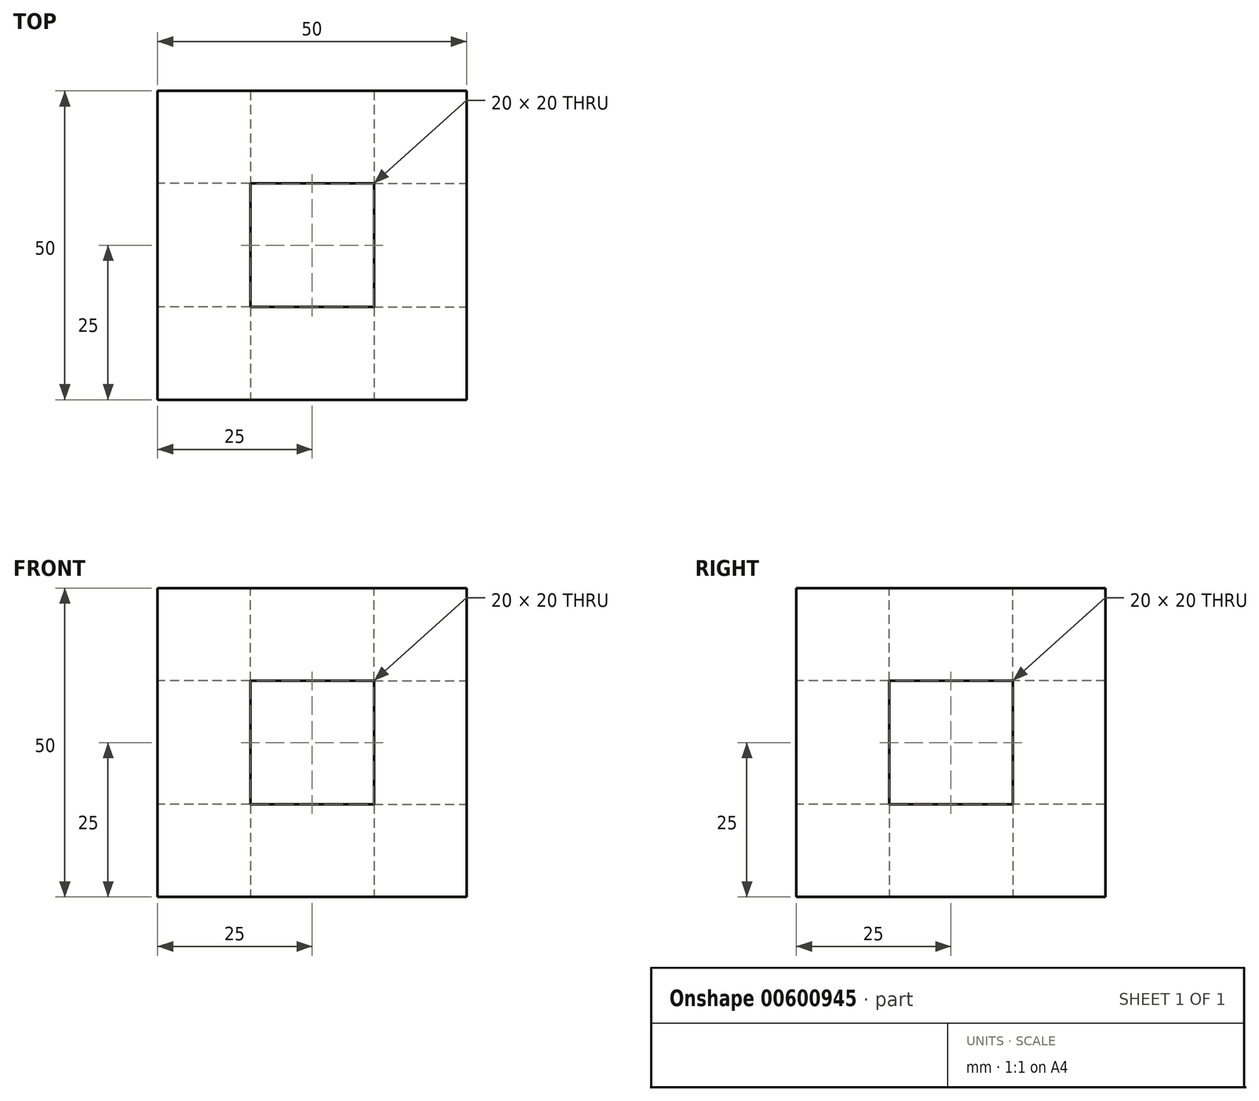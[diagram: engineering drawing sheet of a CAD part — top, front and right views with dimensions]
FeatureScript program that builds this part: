
annotation { "Feature Type Name" : "Feature", "Feature Type Description" : "" }
export const myFeature = defineFeature(function(context is Context, id is Id, definition is map)
    precondition{}
    {
        {
            var Q0;
            Q0=qCreatedBy(makeId("Front.planeOp"),FACE);
            var sketch = newSketch(context, id + "F0", { "sketchPlane" : qUnion([Q0])});
            skLineSegment(sketch, "E0.bottom", {"start": v(25, -25) * mm, "end": v(-25, -25) * mm});
            skLineSegment(sketch, "E0.top", {"start": v(25, 25) * mm, "end": v(-25, 25) * mm});
            skLineSegment(sketch, "E0.left", {"start": v(25, -25) * mm, "end": v(25, 25) * mm});
            skLineSegment(sketch, "E0.right", {"start": v(-25, -25) * mm, "end": v(-25, 25) * mm});
            skPoint(sketch, "E0.middle", {"position": v(0, 0) * mm});
            skSolve(sketch);
        }
        {
            var Q0;
            Q0 = qSketchRegion(id + "F0", true);
            extrude(context, id + "F1", {"entities" : qUnion([Q0]), "endBound" : BoundingType.SYMMETRIC, "depth" : 50 * mm, "offsetDistance" : 25 * mm});
        }
        {
            var Q0;
            Q0=makeQuery(id+"F1.opExtrude","CAP_FACE",FACE,{"disambiguationData":[OSD([sQuery(id+"F0.wireOp",EDGE,"E0.bottom"),sQuery(id+"F0.wireOp",EDGE,"E0.top"),sQuery(id+"F0.wireOp",EDGE,"E0.left"),sQuery(id+"F0.wireOp",EDGE,"E0.right")])],"isStart":false});
            var sketch = newSketch(context, id + "F2", { "sketchPlane" : qUnion([Q0])});
            skLineSegment(sketch, "E1.bottom", {"start": v(10, -10) * mm, "end": v(-10, -10) * mm});
            skLineSegment(sketch, "E1.top", {"start": v(10, 10) * mm, "end": v(-10, 10) * mm});
            skLineSegment(sketch, "E1.left", {"start": v(10, -10) * mm, "end": v(10, 10) * mm});
            skLineSegment(sketch, "E1.right", {"start": v(-10, -10) * mm, "end": v(-10, 10) * mm});
            skPoint(sketch, "E1.middle", {"position": v(0, 0) * mm});
            skSolve(sketch);
        }
        {
            var Q0;
            Q0=makeQuery(id+"F2.imprint","IMPRINT",FACE,{"disambiguationData":[TD([[makeQuery(id+"F2.imprint","IMPRINT",EDGE,{"derivedFrom":sQuery(id+"F2.wireOp",EDGE,"E1.bottom")}),-1.0]])]});
            extrude(context, id + "F3", {"entities" : qUnion([Q0]), "operationType" : NewBodyOperationType.REMOVE, "endBound" : BoundingType.UP_TO_NEXT, "oppositeDirection" : true, "depth" : 25 * mm, "offsetDistance" : 25 * mm});
        }
        {
            var Q0;
            Q0=makeQuery(id+"F1.opExtrude","SWEPT_FACE",FACE,{"disambiguationData":[OSD([sQuery(id+"F0.wireOp",EDGE,"E0.right")])]});
            var sketch = newSketch(context, id + "F4", { "sketchPlane" : qUnion([Q0])});
            skLineSegment(sketch, "E2.bottom", {"start": v(10, -10) * mm, "end": v(-10, -10) * mm});
            skLineSegment(sketch, "E2.top", {"start": v(10, 10) * mm, "end": v(-10, 10) * mm});
            skLineSegment(sketch, "E2.left", {"start": v(10, -10) * mm, "end": v(10, 10) * mm});
            skLineSegment(sketch, "E2.right", {"start": v(-10, -10) * mm, "end": v(-10, 10) * mm});
            skPoint(sketch, "E2.middle", {"position": v(0, 0) * mm});
            skSolve(sketch);
        }
        {
            var Q0;
            Q0 = qSketchRegion(id + "F4", true);
            extrude(context, id + "F5", {"entities" : qUnion([Q0]), "operationType" : NewBodyOperationType.REMOVE, "endBound" : BoundingType.UP_TO_NEXT, "oppositeDirection" : true, "depth" : 25 * mm, "offsetDistance" : 25 * mm});
        }
        {
            var Q0;
            Q0=makeQuery(id+"F1.opExtrude","SWEPT_FACE",FACE,{"disambiguationData":[OSD([sQuery(id+"F0.wireOp",EDGE,"E0.left")])]});
            var sketch = newSketch(context, id + "F6", { "sketchPlane" : qUnion([Q0])});
            skLineSegment(sketch, "E3.bottom", {"start": v(10, -10) * mm, "end": v(-10, -10) * mm});
            skLineSegment(sketch, "E3.top", {"start": v(10, 10) * mm, "end": v(-10, 10) * mm});
            skLineSegment(sketch, "E3.left", {"start": v(10, -10) * mm, "end": v(10, 10) * mm});
            skLineSegment(sketch, "E3.right", {"start": v(-10, -10) * mm, "end": v(-10, 10) * mm});
            skPoint(sketch, "E3.middle", {"position": v(0, 0) * mm});
            skSolve(sketch);
        }
        {
            var Q0;
            Q0 = qSketchRegion(id + "F6", true);
            extrude(context, id + "F7", {"entities" : qUnion([Q0]), "operationType" : NewBodyOperationType.REMOVE, "endBound" : BoundingType.UP_TO_NEXT, "oppositeDirection" : true, "depth" : 25 * mm, "offsetDistance" : 25 * mm});
        }
        {
            var Q0;
            Q0=makeQuery(id+"F1.opExtrude","SWEPT_FACE",FACE,{"disambiguationData":[OSD([sQuery(id+"F0.wireOp",EDGE,"E0.top")])]});
            var sketch = newSketch(context, id + "F8", { "sketchPlane" : qUnion([Q0])});
            skLineSegment(sketch, "E4.bottom", {"start": v(10, -10) * mm, "end": v(-10, -10) * mm});
            skLineSegment(sketch, "E4.top", {"start": v(10, 10) * mm, "end": v(-10, 10) * mm});
            skLineSegment(sketch, "E4.left", {"start": v(10, -10) * mm, "end": v(10, 10) * mm});
            skLineSegment(sketch, "E4.right", {"start": v(-10, -10) * mm, "end": v(-10, 10) * mm});
            skPoint(sketch, "E4.middle", {"position": v(0, 0) * mm});
            skSolve(sketch);
        }
        {
            var Q0;
            Q0 = qSketchRegion(id + "F8", true);
            extrude(context, id + "F9", {"entities" : qUnion([Q0]), "operationType" : NewBodyOperationType.REMOVE, "endBound" : BoundingType.UP_TO_NEXT, "oppositeDirection" : true, "depth" : 25 * mm, "offsetDistance" : 25 * mm});
        }
        {
            var Q0;
            Q0=makeQuery(id+"F1.opExtrude","SWEPT_FACE",FACE,{"disambiguationData":[OSD([sQuery(id+"F0.wireOp",EDGE,"E0.bottom")])]});
            var sketch = newSketch(context, id + "F10", { "sketchPlane" : qUnion([Q0])});
            skLineSegment(sketch, "E5.bottom", {"start": v(10, -10) * mm, "end": v(-10, -10) * mm});
            skLineSegment(sketch, "E5.top", {"start": v(10, 10) * mm, "end": v(-10, 10) * mm});
            skLineSegment(sketch, "E5.left", {"start": v(10, -10) * mm, "end": v(10, 10) * mm});
            skLineSegment(sketch, "E5.right", {"start": v(-10, -10) * mm, "end": v(-10, 10) * mm});
            skPoint(sketch, "E5.middle", {"position": v(0, 0) * mm});
            skSolve(sketch);
        }
        {
            var Q0;
            Q0 = qSketchRegion(id + "F10", true);
            extrude(context, id + "F11", {"entities" : qUnion([Q0]), "operationType" : NewBodyOperationType.REMOVE, "endBound" : BoundingType.UP_TO_NEXT, "oppositeDirection" : true, "depth" : 25 * mm, "offsetDistance" : 25 * mm});
        }
    });
